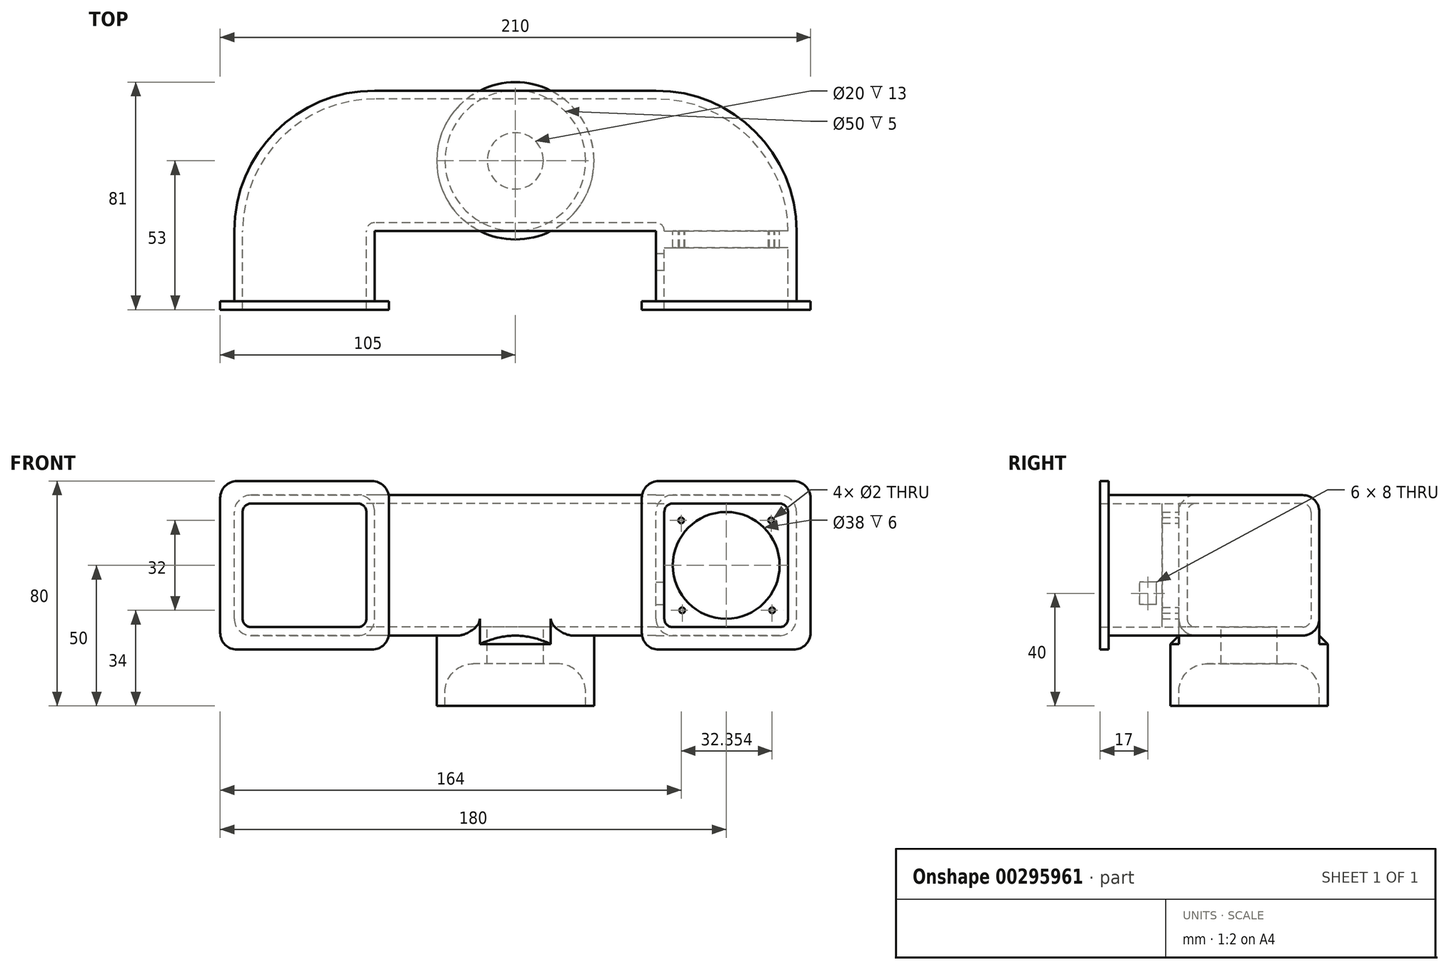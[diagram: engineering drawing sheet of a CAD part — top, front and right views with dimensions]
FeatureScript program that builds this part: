
annotation { "Feature Type Name" : "Feature", "Feature Type Description" : "" }
export const myFeature = defineFeature(function(context is Context, id is Id, definition is map)
    precondition{}
    {
        {
            var Q0;
            Q0=qCreatedBy(makeId("Top.planeOp"),FACE);
            var sketch = newSketch(context, id + "F0", { "sketchPlane" : qUnion([Q0])});
            skCircle(sketch, "E0", {"center": v(0, 0) * mm, "radius": 25 * mm});
            skCircle(sketch, "E1", {"center": v(0, 0) * mm, "radius": 10 * mm});
            skCircle(sketch, "E2", {"center": v(0, 0) * mm, "radius": 28 * mm});
            skSolve(sketch);
        }
        {
            var Q0;
            Q0=qCreatedBy(makeId("Front.planeOp"),FACE);
            var sketch = newSketch(context, id + "F1", { "sketchPlane" : qUnion([Q0])});
            skLineSegment(sketch, "E3", {"start": v(28, 0) * mm, "end": v(25, 0) * mm});
            skLineSegment(sketch, "E4", {"start": v(25, 0) * mm, "end": v(25, 5) * mm});
            skLineSegment(sketch, "E5", {"start": v(15, 15) * mm, "end": v(10, 15) * mm});
            skLineSegment(sketch, "E6", {"start": v(10, 15) * mm, "end": v(10, 25) * mm});
            skLineSegment(sketch, "E7", {"start": v(10, 25) * mm, "end": v(28, 25) * mm});
            skLineSegment(sketch, "E8", {"start": v(28, 25) * mm, "end": v(28, 0) * mm});
            skPoint(sketch, "E9.visualSharp", {"position": v(25, 15) * mm});
            skArc(sketch, "E9.filletArc", {"start": v(25, 5) * mm, "mid": v(22.07, 12.07) * mm, "end": v(15, 15) * mm});
            skLineSegment(sketch, "E10", {"start": v(0, 20.68) * mm, "end": v(0, 0) * mm, "construction": true});
            skSolve(sketch);
        }
        {
            var Q0;
            Q0 = qSketchRegion(id + "F1", true);
            var Q1;
            Q1=sQuery(id+"F1.wireOp",EDGE,"E10");
            revolve(context, id + "F2", {"entities" : qUnion([Q0]), "axis" : qUnion([Q1]), "revolveType" : RevolveType.FULL});
        }
        {
            var Q0;
            Q0=qCreatedBy(makeId("Right.planeOp"),FACE);
            var sketch = newSketch(context, id + "F3", { "sketchPlane" : qUnion([Q0])});
            skLineSegment(sketch, "E11.bottom", {"start": v(25, 25) * mm, "end": v(-25, 25) * mm});
            skLineSegment(sketch, "E11.top", {"start": v(19, 75) * mm, "end": v(-19, 75) * mm});
            skLineSegment(sketch, "E11.left", {"start": v(25, 25) * mm, "end": v(25, 69) * mm});
            skLineSegment(sketch, "E11.right", {"start": v(-25, 25) * mm, "end": v(-25, 69) * mm});
            skLineSegment(sketch, "E12.bottom", {"start": v(-19, 72) * mm, "end": v(19, 72) * mm});
            skLineSegment(sketch, "E12.top", {"start": v(-19, 28) * mm, "end": v(19, 28) * mm});
            skLineSegment(sketch, "E12.left", {"start": v(-22, 69) * mm, "end": v(-22, 31) * mm});
            skLineSegment(sketch, "E12.right", {"start": v(22, 69) * mm, "end": v(22, 31) * mm});
            skLineSegment(sketch, "E13", {"start": v(0, 0) * mm, "end": v(0, 25) * mm, "construction": true});
            skPoint(sketch, "E14.visualSharp", {"position": v(-22, 72) * mm});
            skArc(sketch, "E14.filletArc", {"start": v(-19, 72) * mm, "mid": v(-21.12, 71.12) * mm, "end": v(-22, 69) * mm});
            skPoint(sketch, "E15.visualSharp", {"position": v(22, 72) * mm});
            skArc(sketch, "E15.filletArc", {"start": v(22, 69) * mm, "mid": v(21.12, 71.12) * mm, "end": v(19, 72) * mm});
            skPoint(sketch, "E16.visualSharp", {"position": v(22, 28) * mm});
            skArc(sketch, "E16.filletArc", {"start": v(19, 28) * mm, "mid": v(21.12, 28.88) * mm, "end": v(22, 31) * mm});
            skPoint(sketch, "E17.visualSharp", {"position": v(-22, 28) * mm});
            skArc(sketch, "E17.filletArc", {"start": v(-22, 31) * mm, "mid": v(-21.12, 28.88) * mm, "end": v(-19, 28) * mm});
            skPoint(sketch, "E18.visualSharp", {"position": v(-25, 75) * mm});
            skArc(sketch, "E18.filletArc", {"start": v(-19, 75) * mm, "mid": v(-23.24, 73.24) * mm, "end": v(-25, 69) * mm});
            skPoint(sketch, "E19.visualSharp", {"position": v(25, 75) * mm});
            skArc(sketch, "E19.filletArc", {"start": v(25, 69) * mm, "mid": v(23.24, 73.24) * mm, "end": v(19, 75) * mm});
            skSolve(sketch);
        }
        {
            var Q0;
            Q0 = qSketchRegion(id + "F3", true);
            extrude(context, id + "F4", {"entities" : qUnion([Q0]), "operationType" : NewBodyOperationType.ADD, "endBound" : BoundingType.SYMMETRIC, "depth" : 100 * mm});
        }
        {
            var Q0;
            Q0=makeQuery(id+"F0.imprint","IMPRINT",FACE,{"disambiguationData":[TD([[makeQuery(id+"F0.imprint","IMPRINT",EDGE,{"derivedFrom":sQuery(id+"F0.wireOp",EDGE,"E1")}),1.0]])]});
            var Q1;
            Q1=sQuery(id+"F0.wireOp",EDGE,"E1");
            extrude(context, id + "F5", {"entities" : qUnion([Q0]), "operationType" : NewBodyOperationType.REMOVE, "surfaceEntities" : qUnion([Q1]), "depth" : 50 * mm});
        }
        {
            var Q0;
            {var subQ0=sQuery(id+"F1.wireOp",EDGE,"E7");var subQ1=makeQuery(id+"F2.opRevolve","SWEPT_FACE",FACE,{"disambiguationData":[OSD([subQ0])]});var subQ2=sQuery(id+"F1.wireOp",EDGE,"E8");var subQ3=makeQuery(id+"F2.opRevolve","SWEPT_FACE",FACE,{"disambiguationData":[OSD([subQ2])]});Q0=makeQuery(id+"F4.boolean.opBoolean","SPLIT",EDGE,{"disambiguationData":[topologyDisambiguationEdgeConnected([subQ1,subQ3]),TD([makeQuery(id+"F4.opExtrude","SWEPT_FACE",FACE,{"disambiguationData":[OSD([sQuery(id+"F3.wireOp",EDGE,"E11.right")])]})])],"derivedFrom":makeQuery(id+"F2.opRevolve","SWEPT_EDGE",EDGE,{"disambiguationData":[OSD([subQ0,subQ2])]})});}
            var Q1;
            {var subQ0=sQuery(id+"F1.wireOp",EDGE,"E7");var subQ1=makeQuery(id+"F2.opRevolve","SWEPT_FACE",FACE,{"disambiguationData":[OSD([subQ0])]});var subQ2=sQuery(id+"F1.wireOp",EDGE,"E8");var subQ3=makeQuery(id+"F2.opRevolve","SWEPT_FACE",FACE,{"disambiguationData":[OSD([subQ2])]});Q1=makeQuery(id+"F4.boolean.opBoolean","SPLIT",EDGE,{"disambiguationData":[topologyDisambiguationEdgeConnected([subQ1,subQ3]),TD([makeQuery(id+"F4.opExtrude","SWEPT_FACE",FACE,{"disambiguationData":[OSD([sQuery(id+"F3.wireOp",EDGE,"E11.left")])]})])],"derivedFrom":makeQuery(id+"F2.opRevolve","SWEPT_EDGE",EDGE,{"disambiguationData":[OSD([subQ0,subQ2])]})});}
            chamfer(context, id + "F6", {"entities" : qUnion([Q0, Q1]), "width" : 3 * mm, "tangentPropagation" : true});
        }
        {
            var Q0;
            {var subQ0=sQuery(id+"F3.wireOp",EDGE,"E11.bottom");var subQ1=makeQuery(id+"F4.opExtrude","SWEPT_FACE",FACE,{"disambiguationData":[OSD([subQ0])]});var subQ2=sQuery(id+"F3.wireOp",EDGE,"E11.right");var subQ3=makeQuery(id+"F4.opExtrude","SWEPT_FACE",FACE,{"disambiguationData":[OSD([subQ2])]});Q0=makeQuery(id+"F4.boolean.opBoolean","SPLIT",EDGE,{"disambiguationData":[topologyDisambiguationEdgeConnected([subQ1,subQ3]),TD([makeQuery(id+"F4.opExtrude","CAP_FACE",FACE,{"disambiguationData":[OSD([subQ0,sQuery(id+"F3.wireOp",EDGE,"E11.top"),sQuery(id+"F3.wireOp",EDGE,"E11.left"),subQ2,sQuery(id+"F3.wireOp",EDGE,"E12.bottom"),sQuery(id+"F3.wireOp",EDGE,"E12.top"),sQuery(id+"F3.wireOp",EDGE,"E12.left"),sQuery(id+"F3.wireOp",EDGE,"E12.right"),sQuery(id+"F3.wireOp",EDGE,"E14.filletArc"),sQuery(id+"F3.wireOp",EDGE,"E15.filletArc"),sQuery(id+"F3.wireOp",EDGE,"E16.filletArc"),sQuery(id+"F3.wireOp",EDGE,"E17.filletArc"),sQuery(id+"F3.wireOp",EDGE,"E18.filletArc"),sQuery(id+"F3.wireOp",EDGE,"E19.filletArc")])],"isStart":false})])],"derivedFrom":makeQuery(id+"F4.opExtrude","SWEPT_EDGE",EDGE,{"disambiguationData":[OSD([subQ0,subQ2])]})});}
            var Q1;
            {var subQ0=sQuery(id+"F3.wireOp",EDGE,"E11.bottom");var subQ1=makeQuery(id+"F4.opExtrude","SWEPT_FACE",FACE,{"disambiguationData":[OSD([subQ0])]});var subQ2=sQuery(id+"F3.wireOp",EDGE,"E11.left");var subQ3=makeQuery(id+"F4.opExtrude","SWEPT_FACE",FACE,{"disambiguationData":[OSD([subQ2])]});Q1=makeQuery(id+"F4.boolean.opBoolean","SPLIT",EDGE,{"disambiguationData":[topologyDisambiguationEdgeConnected([subQ1,subQ3]),TD([makeQuery(id+"F4.opExtrude","CAP_FACE",FACE,{"disambiguationData":[OSD([subQ0,sQuery(id+"F3.wireOp",EDGE,"E11.top"),subQ2,sQuery(id+"F3.wireOp",EDGE,"E11.right"),sQuery(id+"F3.wireOp",EDGE,"E12.bottom"),sQuery(id+"F3.wireOp",EDGE,"E12.top"),sQuery(id+"F3.wireOp",EDGE,"E12.left"),sQuery(id+"F3.wireOp",EDGE,"E12.right"),sQuery(id+"F3.wireOp",EDGE,"E14.filletArc"),sQuery(id+"F3.wireOp",EDGE,"E15.filletArc"),sQuery(id+"F3.wireOp",EDGE,"E16.filletArc"),sQuery(id+"F3.wireOp",EDGE,"E17.filletArc"),sQuery(id+"F3.wireOp",EDGE,"E18.filletArc"),sQuery(id+"F3.wireOp",EDGE,"E19.filletArc")])],"isStart":false})])],"derivedFrom":makeQuery(id+"F4.opExtrude","SWEPT_EDGE",EDGE,{"disambiguationData":[OSD([subQ0,subQ2])]})});}
            var Q2;
            {var subQ0=sQuery(id+"F3.wireOp",EDGE,"E11.bottom");var subQ1=makeQuery(id+"F4.opExtrude","SWEPT_FACE",FACE,{"disambiguationData":[OSD([subQ0])]});var subQ2=sQuery(id+"F3.wireOp",EDGE,"E11.right");var subQ3=makeQuery(id+"F4.opExtrude","SWEPT_FACE",FACE,{"disambiguationData":[OSD([subQ2])]});Q2=makeQuery(id+"F4.boolean.opBoolean","SPLIT",EDGE,{"disambiguationData":[topologyDisambiguationEdgeConnected([subQ1,subQ3]),TD([makeQuery(id+"F4.opExtrude","CAP_FACE",FACE,{"disambiguationData":[OSD([subQ0,sQuery(id+"F3.wireOp",EDGE,"E11.top"),sQuery(id+"F3.wireOp",EDGE,"E11.left"),subQ2,sQuery(id+"F3.wireOp",EDGE,"E12.bottom"),sQuery(id+"F3.wireOp",EDGE,"E12.top"),sQuery(id+"F3.wireOp",EDGE,"E12.left"),sQuery(id+"F3.wireOp",EDGE,"E12.right"),sQuery(id+"F3.wireOp",EDGE,"E14.filletArc"),sQuery(id+"F3.wireOp",EDGE,"E15.filletArc"),sQuery(id+"F3.wireOp",EDGE,"E16.filletArc"),sQuery(id+"F3.wireOp",EDGE,"E17.filletArc"),sQuery(id+"F3.wireOp",EDGE,"E18.filletArc"),sQuery(id+"F3.wireOp",EDGE,"E19.filletArc")])],"isStart":true})])],"derivedFrom":makeQuery(id+"F4.opExtrude","SWEPT_EDGE",EDGE,{"disambiguationData":[OSD([subQ0,subQ2])]})});}
            var Q3;
            {var subQ0=sQuery(id+"F3.wireOp",EDGE,"E11.bottom");var subQ1=makeQuery(id+"F4.opExtrude","SWEPT_FACE",FACE,{"disambiguationData":[OSD([subQ0])]});var subQ2=sQuery(id+"F3.wireOp",EDGE,"E11.left");var subQ3=makeQuery(id+"F4.opExtrude","SWEPT_FACE",FACE,{"disambiguationData":[OSD([subQ2])]});Q3=makeQuery(id+"F4.boolean.opBoolean","SPLIT",EDGE,{"disambiguationData":[topologyDisambiguationEdgeConnected([subQ1,subQ3]),TD([makeQuery(id+"F4.opExtrude","CAP_FACE",FACE,{"disambiguationData":[OSD([subQ0,sQuery(id+"F3.wireOp",EDGE,"E11.top"),subQ2,sQuery(id+"F3.wireOp",EDGE,"E11.right"),sQuery(id+"F3.wireOp",EDGE,"E12.bottom"),sQuery(id+"F3.wireOp",EDGE,"E12.top"),sQuery(id+"F3.wireOp",EDGE,"E12.left"),sQuery(id+"F3.wireOp",EDGE,"E12.right"),sQuery(id+"F3.wireOp",EDGE,"E14.filletArc"),sQuery(id+"F3.wireOp",EDGE,"E15.filletArc"),sQuery(id+"F3.wireOp",EDGE,"E16.filletArc"),sQuery(id+"F3.wireOp",EDGE,"E17.filletArc"),sQuery(id+"F3.wireOp",EDGE,"E18.filletArc"),sQuery(id+"F3.wireOp",EDGE,"E19.filletArc")])],"isStart":true})])],"derivedFrom":makeQuery(id+"F4.opExtrude","SWEPT_EDGE",EDGE,{"disambiguationData":[OSD([subQ0,subQ2])]})});}
            fillet(context, id + "F7", {"entities" : qUnion([Q0, Q1, Q2, Q3]), "radius" : 6 * mm, "tangentPropagation" : true, "allowEdgeOverflow" : false});
        }
        {
            var Q0;
            Q0=qCreatedBy(makeId("Front.planeOp"),FACE);
            cPlane(context, id + "F8", {"entities" : qUnion([Q0]), "cplaneType" : CPlaneType.OFFSET, "offset" : 25 * mm, "width" : 150 * mm, "height" : 150 * mm});
        }
        {
            var Q0;
            Q0=qCreatedBy(id+"F8.planeOp",FACE);
            var sketch = newSketch(context, id + "F9", { "sketchPlane" : qUnion([Q0])});
            skLineSegment(sketch, "E20.bottom", {"start": v(94, 25) * mm, "end": v(56, 25) * mm});
            skLineSegment(sketch, "E20.top", {"start": v(94, 75) * mm, "end": v(56, 75) * mm});
            skLineSegment(sketch, "E20.left", {"start": v(100, 31) * mm, "end": v(100, 69) * mm});
            skLineSegment(sketch, "E20.right", {"start": v(50, 31) * mm, "end": v(50, 69) * mm});
            skLineSegment(sketch, "E21.bottom", {"start": v(56, 72) * mm, "end": v(94, 72) * mm});
            skLineSegment(sketch, "E21.top", {"start": v(56, 28) * mm, "end": v(94, 28) * mm});
            skLineSegment(sketch, "E21.left", {"start": v(53, 69) * mm, "end": v(53, 31) * mm});
            skLineSegment(sketch, "E21.right", {"start": v(97, 69) * mm, "end": v(97, 31) * mm});
            skLineSegment(sketch, "E22", {"start": v(75, 0) * mm, "end": v(75, 25) * mm, "construction": true});
            skPoint(sketch, "E23.visualSharp", {"position": v(53, 72) * mm});
            skArc(sketch, "E23.filletArc", {"start": v(56, 72) * mm, "mid": v(53.88, 71.12) * mm, "end": v(53, 69) * mm});
            skPoint(sketch, "E24.visualSharp", {"position": v(97, 72) * mm});
            skArc(sketch, "E24.filletArc", {"start": v(97, 69) * mm, "mid": v(96.12, 71.12) * mm, "end": v(94, 72) * mm});
            skPoint(sketch, "E25.visualSharp", {"position": v(97, 28) * mm});
            skArc(sketch, "E25.filletArc", {"start": v(94, 28) * mm, "mid": v(96.12, 28.88) * mm, "end": v(97, 31) * mm});
            skPoint(sketch, "E26.visualSharp", {"position": v(53, 28) * mm});
            skArc(sketch, "E26.filletArc", {"start": v(53, 31) * mm, "mid": v(53.88, 28.88) * mm, "end": v(56, 28) * mm});
            skPoint(sketch, "E27.visualSharp", {"position": v(50, 75) * mm});
            skArc(sketch, "E27.filletArc", {"start": v(56, 75) * mm, "mid": v(51.76, 73.24) * mm, "end": v(50, 69) * mm});
            skPoint(sketch, "E28.visualSharp", {"position": v(100, 75) * mm});
            skArc(sketch, "E28.filletArc", {"start": v(100, 69) * mm, "mid": v(98.24, 73.24) * mm, "end": v(94, 75) * mm});
            skPoint(sketch, "E29.visualSharp", {"position": v(50, 25) * mm});
            skArc(sketch, "E29.filletArc", {"start": v(50, 31) * mm, "mid": v(51.76, 26.76) * mm, "end": v(56, 25) * mm});
            skPoint(sketch, "E30.visualSharp", {"position": v(100, 25) * mm});
            skArc(sketch, "E30.filletArc", {"start": v(94, 25) * mm, "mid": v(98.24, 26.76) * mm, "end": v(100, 31) * mm});
            skLineSegment(sketch, "E31", {"start": v(0, 0) * mm, "end": v(0, 40.23) * mm, "construction": true});
            skArc(sketch, "E32.MirrorCS", {"start": v(-53, 31) * mm, "mid": v(-53.88, 28.88) * mm, "end": v(-56, 28) * mm});
            skArc(sketch, "E33.MirrorCS", {"start": v(-56, 72) * mm, "mid": v(-53.88, 71.12) * mm, "end": v(-53, 69) * mm});
            skArc(sketch, "E34.MirrorCS", {"start": v(-94, 28) * mm, "mid": v(-96.12, 28.88) * mm, "end": v(-97, 31) * mm});
            skArc(sketch, "E35.MirrorCS", {"start": v(-97, 69) * mm, "mid": v(-96.12, 71.12) * mm, "end": v(-94, 72) * mm});
            skArc(sketch, "E36.MirrorCS", {"start": v(-56, 75) * mm, "mid": v(-51.76, 73.24) * mm, "end": v(-50, 69) * mm});
            skArc(sketch, "E37.MirrorCS", {"start": v(-100, 69) * mm, "mid": v(-98.24, 73.24) * mm, "end": v(-94, 75) * mm});
            skArc(sketch, "E38.MirrorCS", {"start": v(-50, 31) * mm, "mid": v(-51.76, 26.76) * mm, "end": v(-56, 25) * mm});
            skArc(sketch, "E39.MirrorCS", {"start": v(-94, 25) * mm, "mid": v(-98.24, 26.76) * mm, "end": v(-100, 31) * mm});
            skPoint(sketch, "E40.MirrorP", {"position": v(-53, 28) * mm});
            skPoint(sketch, "E41.MirrorP", {"position": v(-97, 72) * mm});
            skPoint(sketch, "E42.MirrorP", {"position": v(-53, 72) * mm});
            skLineSegment(sketch, "E43.MirrorCS", {"start": v(-94, 25) * mm, "end": v(-56, 25) * mm});
            skLineSegment(sketch, "E44.MirrorCS", {"start": v(-94, 75) * mm, "end": v(-56, 75) * mm});
            skLineSegment(sketch, "E45.MirrorCS", {"start": v(-100, 31) * mm, "end": v(-100, 69) * mm});
            skLineSegment(sketch, "E46.MirrorCS", {"start": v(-50, 31) * mm, "end": v(-50, 69) * mm});
            skLineSegment(sketch, "E47.MirrorCS", {"start": v(-56, 72) * mm, "end": v(-94, 72) * mm});
            skLineSegment(sketch, "E48.MirrorCS", {"start": v(-56, 28) * mm, "end": v(-94, 28) * mm});
            skLineSegment(sketch, "E49.MirrorCS", {"start": v(-53, 69) * mm, "end": v(-53, 31) * mm});
            skLineSegment(sketch, "E50.MirrorCS", {"start": v(-97, 69) * mm, "end": v(-97, 31) * mm});
            skLineSegment(sketch, "E51.MirrorCS", {"start": v(-75, 0) * mm, "end": v(-75, 25) * mm, "construction": true});
            skPoint(sketch, "E52.MirrorP", {"position": v(-100, 25) * mm});
            skPoint(sketch, "E53.MirrorP", {"position": v(-50, 25) * mm});
            skPoint(sketch, "E54.MirrorP", {"position": v(-100, 75) * mm});
            skPoint(sketch, "E55.MirrorP", {"position": v(-50, 75) * mm});
            skPoint(sketch, "E56.MirrorP", {"position": v(-97, 28) * mm});
            skLineSegment(sketch, "E57", {"start": v(-50, 25) * mm, "end": v(-50, 75) * mm, "construction": true});
            skLineSegment(sketch, "E58", {"start": v(50, 25) * mm, "end": v(50, 75) * mm, "construction": true});
            skSolve(sketch);
        }
        {
            var Q0;
            Q0 = qSketchRegion(id + "F9", true);
            extrude(context, id + "F10", {"entities" : qUnion([Q0]), "operationType" : NewBodyOperationType.ADD, "depth" : 25 * mm});
        }
        {
            var Q0;
            Q0=makeQuery(id+"F10.opExtrude","CAP_FACE",FACE,{"disambiguationData":[OSD([sQuery(id+"F9.wireOp",EDGE,"E32.MirrorCS"),sQuery(id+"F9.wireOp",EDGE,"E33.MirrorCS"),sQuery(id+"F9.wireOp",EDGE,"E34.MirrorCS"),sQuery(id+"F9.wireOp",EDGE,"E35.MirrorCS"),sQuery(id+"F9.wireOp",EDGE,"E36.MirrorCS"),sQuery(id+"F9.wireOp",EDGE,"E37.MirrorCS"),sQuery(id+"F9.wireOp",EDGE,"E38.MirrorCS"),sQuery(id+"F9.wireOp",EDGE,"E39.MirrorCS"),sQuery(id+"F9.wireOp",EDGE,"E43.MirrorCS"),sQuery(id+"F9.wireOp",EDGE,"E44.MirrorCS"),sQuery(id+"F9.wireOp",EDGE,"E45.MirrorCS"),sQuery(id+"F9.wireOp",EDGE,"E46.MirrorCS"),sQuery(id+"F9.wireOp",EDGE,"E47.MirrorCS"),sQuery(id+"F9.wireOp",EDGE,"E48.MirrorCS"),sQuery(id+"F9.wireOp",EDGE,"E49.MirrorCS"),sQuery(id+"F9.wireOp",EDGE,"E50.MirrorCS")])],"isStart":true});
            var Q1;
            Q1=sQuery(id+"F9.wireOp",EDGE,"E57");
            revolve(context, id + "F11", {"operationType" : NewBodyOperationType.ADD, "entities" : qUnion([Q0]), "axis" : qUnion([Q1]), "revolveType" : RevolveType.ONE_DIRECTION, "oppositeDirection" : true, "angle" : 90 * degree});
        }
        {
            var Q0;
            Q0=makeQuery(id+"F9.imprint","IMPRINT",FACE,{"disambiguationData":[TD([[makeQuery(id+"F9.imprint","IMPRINT",EDGE,{"derivedFrom":sQuery(id+"F9.wireOp",EDGE,"E20.bottom")}),-1.0]])]});
            var Q1;
            Q1=sQuery(id+"F9.wireOp",EDGE,"E58");
            revolve(context, id + "F12", {"operationType" : NewBodyOperationType.ADD, "entities" : qUnion([Q0]), "axis" : qUnion([Q1]), "revolveType" : RevolveType.ONE_DIRECTION, "angle" : 90 * degree});
        }
        {
            var Q0;
            Q0=makeQuery(id+"F10.opExtrude","CAP_FACE",FACE,{"disambiguationData":[OSD([sQuery(id+"F9.wireOp",EDGE,"E20.bottom"),sQuery(id+"F9.wireOp",EDGE,"E20.top"),sQuery(id+"F9.wireOp",EDGE,"E20.left"),sQuery(id+"F9.wireOp",EDGE,"E20.right"),sQuery(id+"F9.wireOp",EDGE,"E21.bottom"),sQuery(id+"F9.wireOp",EDGE,"E21.top"),sQuery(id+"F9.wireOp",EDGE,"E21.left"),sQuery(id+"F9.wireOp",EDGE,"E21.right"),sQuery(id+"F9.wireOp",EDGE,"E23.filletArc"),sQuery(id+"F9.wireOp",EDGE,"E24.filletArc"),sQuery(id+"F9.wireOp",EDGE,"E25.filletArc"),sQuery(id+"F9.wireOp",EDGE,"E26.filletArc"),sQuery(id+"F9.wireOp",EDGE,"E27.filletArc"),sQuery(id+"F9.wireOp",EDGE,"E28.filletArc"),sQuery(id+"F9.wireOp",EDGE,"E29.filletArc"),sQuery(id+"F9.wireOp",EDGE,"E30.filletArc")])],"isStart":false});
            var sketch = newSketch(context, id + "F13", { "sketchPlane" : qUnion([Q0])});
            skLineSegment(sketch, "E59.bottom", {"start": v(51, 80) * mm, "end": v(99, 80) * mm});
            skLineSegment(sketch, "E59.top", {"start": v(51, 20) * mm, "end": v(99, 20) * mm});
            skLineSegment(sketch, "E59.left", {"start": v(45, 74) * mm, "end": v(45, 26) * mm});
            skLineSegment(sketch, "E59.right", {"start": v(105, 74) * mm, "end": v(105, 26) * mm});
            skLineSegment(sketch, "E60.bottom", {"start": v(56, 72) * mm, "end": v(94, 72) * mm});
            skLineSegment(sketch, "E60.top", {"start": v(56, 28) * mm, "end": v(94, 28) * mm});
            skLineSegment(sketch, "E60.left", {"start": v(53, 69) * mm, "end": v(53, 31) * mm});
            skLineSegment(sketch, "E60.right", {"start": v(97, 69) * mm, "end": v(97, 31) * mm});
            skPoint(sketch, "E61.visualSharp", {"position": v(45, 80) * mm});
            skArc(sketch, "E61.filletArc", {"start": v(51, 80) * mm, "mid": v(46.76, 78.24) * mm, "end": v(45, 74) * mm});
            skPoint(sketch, "E62.visualSharp", {"position": v(105, 80) * mm});
            skArc(sketch, "E62.filletArc", {"start": v(105, 74) * mm, "mid": v(103.24, 78.24) * mm, "end": v(99, 80) * mm});
            skPoint(sketch, "E63.visualSharp", {"position": v(45, 20) * mm});
            skArc(sketch, "E63.filletArc", {"start": v(45, 26) * mm, "mid": v(46.76, 21.76) * mm, "end": v(51, 20) * mm});
            skPoint(sketch, "E64.visualSharp", {"position": v(105, 20) * mm});
            skArc(sketch, "E64.filletArc", {"start": v(99, 20) * mm, "mid": v(103.24, 21.76) * mm, "end": v(105, 26) * mm});
            skPoint(sketch, "E65.visualSharp", {"position": v(53, 28) * mm});
            skArc(sketch, "E65.filletArc", {"start": v(53, 31) * mm, "mid": v(53.88, 28.88) * mm, "end": v(56, 28) * mm});
            skPoint(sketch, "E66.visualSharp", {"position": v(97, 28) * mm});
            skArc(sketch, "E66.filletArc", {"start": v(94, 28) * mm, "mid": v(96.12, 28.88) * mm, "end": v(97, 31) * mm});
            skPoint(sketch, "E67.visualSharp", {"position": v(97, 72) * mm});
            skArc(sketch, "E67.filletArc", {"start": v(97, 69) * mm, "mid": v(96.12, 71.12) * mm, "end": v(94, 72) * mm});
            skPoint(sketch, "E68.visualSharp", {"position": v(53, 72) * mm});
            skArc(sketch, "E68.filletArc", {"start": v(56, 72) * mm, "mid": v(53.88, 71.12) * mm, "end": v(53, 69) * mm});
            skLineSegment(sketch, "E69.MirrorCS", {"start": v(-105, 74) * mm, "end": v(-105, 26) * mm});
            skArc(sketch, "E70.MirrorCS", {"start": v(-105, 74) * mm, "mid": v(-103.24, 78.24) * mm, "end": v(-99, 80) * mm});
            skLineSegment(sketch, "E71.MirrorCS", {"start": v(-51, 80) * mm, "end": v(-99, 80) * mm});
            skLineSegment(sketch, "E72.MirrorCS", {"start": v(-56, 72) * mm, "end": v(-94, 72) * mm});
            skLineSegment(sketch, "E73.MirrorCS", {"start": v(-45, 74) * mm, "end": v(-45, 26) * mm});
            skLineSegment(sketch, "E74.MirrorCS", {"start": v(-51, 20) * mm, "end": v(-99, 20) * mm});
            skArc(sketch, "E75.MirrorCS", {"start": v(-45, 26) * mm, "mid": v(-46.76, 21.76) * mm, "end": v(-51, 20) * mm});
            skArc(sketch, "E76.MirrorCS", {"start": v(-99, 20) * mm, "mid": v(-103.24, 21.76) * mm, "end": v(-105, 26) * mm});
            skLineSegment(sketch, "E77.MirrorCS", {"start": v(-53, 69) * mm, "end": v(-53, 31) * mm});
            skLineSegment(sketch, "E78.MirrorCS", {"start": v(-56, 28) * mm, "end": v(-94, 28) * mm});
            skLineSegment(sketch, "E79.MirrorCS", {"start": v(-97, 69) * mm, "end": v(-97, 31) * mm});
            skArc(sketch, "E80.MirrorCS", {"start": v(-56, 72) * mm, "mid": v(-53.88, 71.12) * mm, "end": v(-53, 69) * mm});
            skArc(sketch, "E81.MirrorCS", {"start": v(-97, 69) * mm, "mid": v(-96.12, 71.12) * mm, "end": v(-94, 72) * mm});
            skArc(sketch, "E82.MirrorCS", {"start": v(-53, 31) * mm, "mid": v(-53.88, 28.88) * mm, "end": v(-56, 28) * mm});
            skArc(sketch, "E83.MirrorCS", {"start": v(-94, 28) * mm, "mid": v(-96.12, 28.88) * mm, "end": v(-97, 31) * mm});
            skArc(sketch, "E84.MirrorCS", {"start": v(-51, 80) * mm, "mid": v(-46.76, 78.24) * mm, "end": v(-45, 74) * mm});
            skSolve(sketch);
        }
        {
            var Q0;
            Q0 = qSketchRegion(id + "F13", true);
            extrude(context, id + "F14", {"entities" : qUnion([Q0]), "operationType" : NewBodyOperationType.ADD, "depth" : 3 * mm});
        }
        {
            var Q0;
            Q0=makeQuery(id+"F4.opExtrude","SWEPT_FACE",FACE,{"disambiguationData":[OSD([sQuery(id+"F3.wireOp",EDGE,"E11.right")])]});
            var sketch = newSketch(context, id + "F15", { "sketchPlane" : qUnion([Q0])});
            skLineSegment(sketch, "E85.bottom", {"start": v(56, 72) * mm, "end": v(94, 72) * mm});
            skLineSegment(sketch, "E85.top", {"start": v(56, 28) * mm, "end": v(94, 28) * mm});
            skLineSegment(sketch, "E85.left", {"start": v(53, 69) * mm, "end": v(53, 31) * mm});
            skLineSegment(sketch, "E85.right", {"start": v(97, 69) * mm, "end": v(97, 31) * mm});
            skPoint(sketch, "E86.visualSharp", {"position": v(53, 72) * mm});
            skArc(sketch, "E86.filletArc", {"start": v(56, 72) * mm, "mid": v(53.88, 71.12) * mm, "end": v(53, 69) * mm});
            skPoint(sketch, "E87.visualSharp", {"position": v(97, 72) * mm});
            skArc(sketch, "E87.filletArc", {"start": v(97, 69) * mm, "mid": v(96.12, 71.12) * mm, "end": v(94, 72) * mm});
            skPoint(sketch, "E88.visualSharp", {"position": v(97, 28) * mm});
            skArc(sketch, "E88.filletArc", {"start": v(94, 28) * mm, "mid": v(96.12, 28.88) * mm, "end": v(97, 31) * mm});
            skPoint(sketch, "E89.visualSharp", {"position": v(53, 28) * mm});
            skArc(sketch, "E89.filletArc", {"start": v(53, 31) * mm, "mid": v(53.88, 28.88) * mm, "end": v(56, 28) * mm});
            skCircle(sketch, "E90", {"center": v(75, 50) * mm, "radius": 19 * mm});
            skCircle(sketch, "E91", {"center": v(59, 66) * mm, "radius": 1 * mm});
            skCircle(sketch, "E92", {"center": v(91, 66) * mm, "radius": 1 * mm});
            skCircle(sketch, "E93", {"center": v(91.35, 34) * mm, "radius": 1 * mm});
            skCircle(sketch, "E94", {"center": v(59.35, 34) * mm, "radius": 1 * mm});
            skSolve(sketch);
        }
        {
            var Q0;
            Q0 = qSketchRegion(id + "F15", true);
            extrude(context, id + "F16", {"entities" : qUnion([Q0]), "operationType" : NewBodyOperationType.ADD, "depth" : 6 * mm});
        }
        {
            var Q0;
            Q0=makeQuery(id+"F14.boolean.opBoolean","MERGE",FACE,{"derivedFrom":[makeQuery(id+"F10.opExtrude","SWEPT_FACE",FACE,{"disambiguationData":[OSD([sQuery(id+"F9.wireOp",EDGE,"E21.left")])]}),makeQuery(id+"F14.opExtrude","SWEPT_FACE",FACE,{"disambiguationData":[OSD([sQuery(id+"F13.wireOp",EDGE,"E60.left")])]})]});
            var sketch = newSketch(context, id + "F17", { "sketchPlane" : qUnion([Q0])});
            skLineSegment(sketch, "E95.bottom", {"start": v(-39, 44) * mm, "end": v(-33, 44) * mm});
            skLineSegment(sketch, "E95.top", {"start": v(-39, 36) * mm, "end": v(-33, 36) * mm});
            skLineSegment(sketch, "E95.left", {"start": v(-39, 44) * mm, "end": v(-39, 36) * mm});
            skLineSegment(sketch, "E95.right", {"start": v(-33, 44) * mm, "end": v(-33, 36) * mm});
            skSolve(sketch);
        }
        {
            var Q0;
            Q0 = qSketchRegion(id + "F17", true);
            extrude(context, id + "F18", {"entities" : qUnion([Q0]), "operationType" : NewBodyOperationType.REMOVE, "oppositeDirection" : true, "depth" : 4 * mm});
        }
    });
